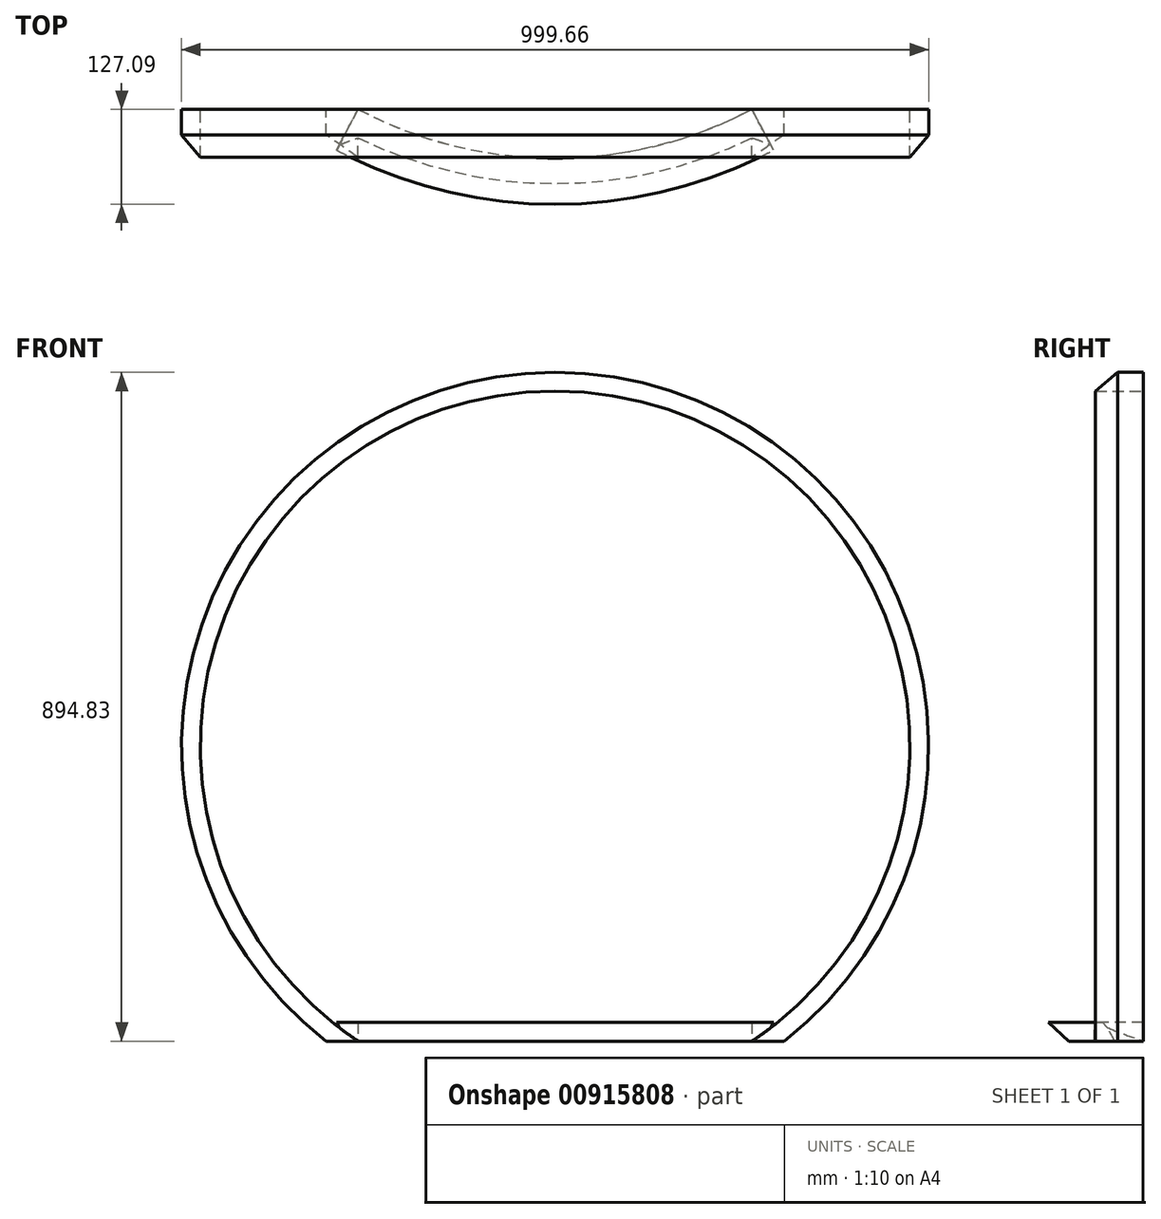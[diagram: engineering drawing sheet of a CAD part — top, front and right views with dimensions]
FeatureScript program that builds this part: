
annotation { "Feature Type Name" : "Feature", "Feature Type Description" : "" }
export const myFeature = defineFeature(function(context is Context, id is Id, definition is map)
    precondition{}
    {
        {
            var Q0;
            Q0=qCreatedBy(makeId("Front.planeOp"),FACE);
            var sketch = newSketch(context, id + "F0", { "sketchPlane" : qUnion([Q0])});
            skArc(sketch, "E0", {"start": v(-108.05, -488.19) * mm, "mid": v(12.85, 499.83) * mm, "end": v(82.82, -493.1) * mm});
            skSolve(sketch);
        }
        {
            var Q0;
            Q0=qCreatedBy(makeId("Right.planeOp"),FACE);
            var sketch = newSketch(context, id + "F1", { "sketchPlane" : qUnion([Q0])});
            skLineSegment(sketch, "E1", {"start": v(95.15, 0) * mm, "end": v(-91.69, 0) * mm, "construction": true});
            skLineSegment(sketch, "E2", {"start": v(0, 499.83) * mm, "end": v(-34.02, 499.83) * mm});
            skLineSegment(sketch, "E3", {"start": v(-34.02, 499.83) * mm, "end": v(-63.87, 474.83) * mm});
            skLineSegment(sketch, "E4", {"start": v(-63.87, 474.83) * mm, "end": v(0, 474.83) * mm});
            skLineSegment(sketch, "E5", {"start": v(0, 499.83) * mm, "end": v(0, 474.83) * mm});
            skSolve(sketch);
        }
        {
            var Q0;
            Q0=makeQuery(id+"F1.imprint","IMPRINT",FACE,{"disambiguationData":[TD([[makeQuery(id+"F1.imprint","IMPRINT",EDGE,{"derivedFrom":sQuery(id+"F1.wireOp",EDGE,"E2")}),1.0]])]});
            var Q1;
            Q1=sQuery(id+"F1.wireOp",EDGE,"E1");
            revolve(context, id + "F2", {"surfaceOperationType" : NewSurfaceOperationType.NEW, "entities" : qUnion([Q0]), "axis" : qUnion([Q1]), "revolveType" : RevolveType.FULL});
        }
        {
            var Q0;
            Q0=qCreatedBy(makeId("Front.planeOp"),FACE);
            var sketch = newSketch(context, id + "F3", { "sketchPlane" : qUnion([Q0])});
            skLineSegment(sketch, "E6", {"start": v(0, 500) * mm, "end": v(0, -395) * mm, "construction": true});
            skLineSegment(sketch, "E7.bottom", {"start": v(-335.98, -395) * mm, "end": v(337.84, -395) * mm});
            skLineSegment(sketch, "E7.top", {"start": v(-335.98, -509) * mm, "end": v(337.84, -509) * mm});
            skLineSegment(sketch, "E7.left", {"start": v(-335.98, -395) * mm, "end": v(-335.98, -509) * mm});
            skLineSegment(sketch, "E7.right", {"start": v(337.84, -395) * mm, "end": v(337.84, -509) * mm});
            skSolve(sketch);
        }
        {
            var Q0;
            Q0 = qSketchRegion(id + "F3", true);
            extrude(context, id + "F4", {"entities" : qUnion([Q0]), "operationType" : NewBodyOperationType.REMOVE, "depth" : 253 * mm, "offsetDistance" : 25 * mm});
        }
        {
            var Q0;
            Q0=qCreatedBy(makeId("Top.planeOp"),FACE);
            cPlane(context, id + "F5", {"entities" : qUnion([Q0]), "cplaneType" : CPlaneType.OFFSET, "offset" : 395 * mm, "oppositeDirection" : true, "width" : 150 * mm, "height" : 150 * mm});
        }
        {
            var Q0;
            Q0=qCreatedBy(id+"F5.planeOp",FACE);
            var sketch = newSketch(context, id + "F6", { "sketchPlane" : qUnion([Q0])});
            skLineSegment(sketch, "E8", {"start": v(306.28, -34.02) * mm, "end": v(-326.37, -34.02) * mm, "construction": true});
            skLineSegment(sketch, "E9", {"start": v(0, -34.02) * mm, "end": v(0, 499.29) * mm, "construction": true});
            skLineSegment(sketch, "E10", {"start": v(0, 499.29) * mm, "end": v(306.28, -34.02) * mm, "construction": true});
            skArc(sketch, "E11", {"start": v(300.44, -7.98) * mm, "mid": v(39.7, -88.94) * mm, "end": v(-229.56, -43.75) * mm});
            skArc(sketch, "E12.0", {"start": v(263.52, 0) * mm, "mid": v(0, -65.28) * mm, "end": v(-263.52, 0) * mm});
            skSolve(sketch);
        }
        {
            var Q0;
            Q0=qCreatedBy(makeId("Right.planeOp"),FACE);
            var sketch = newSketch(context, id + "F7", { "sketchPlane" : qUnion([Q0])});
            skLineSegment(sketch, "E13", {"start": v(-65.28, -370) * mm, "end": v(-65.28, -395) * mm});
            skLineSegment(sketch, "E14", {"start": v(-65.28, -395) * mm, "end": v(-99.3, -395) * mm});
            skLineSegment(sketch, "E15", {"start": v(-65.28, -370) * mm, "end": v(-127.09, -370) * mm});
            skLineSegment(sketch, "E16", {"start": v(-127.09, -370) * mm, "end": v(-99.3, -395) * mm});
            skSolve(sketch);
        }
        {
            var Q0;
            Q0=makeQuery(id+"F7.imprint","IMPRINT",FACE,{"disambiguationData":[TD([[makeQuery(id+"F7.imprint","IMPRINT",EDGE,{"derivedFrom":sQuery(id+"F7.wireOp",EDGE,"E13")}),-1.0]])]});
            var Q1;
            Q1=sQuery(id+"F6.wireOp",EDGE,"E12.0");
            sweep(context, id + "F8", {"operationType" : NewBodyOperationType.ADD, "profiles" : qUnion([Q0]), "path" : qUnion([Q1])});
        }
    });
